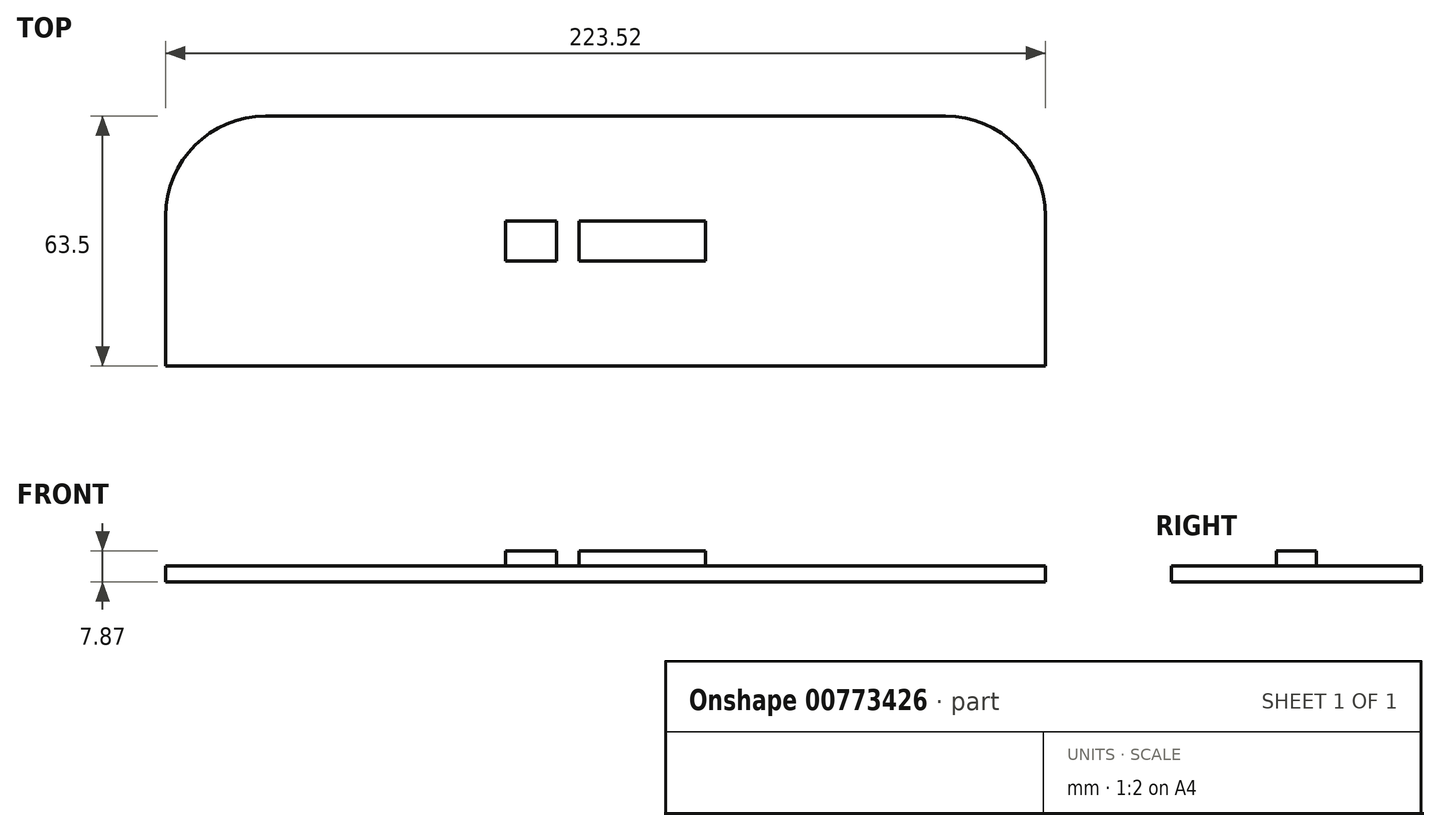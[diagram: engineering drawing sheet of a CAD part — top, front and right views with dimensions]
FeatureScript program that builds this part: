
annotation { "Feature Type Name" : "Feature", "Feature Type Description" : "" }
export const myFeature = defineFeature(function(context is Context, id is Id, definition is map)
    precondition{}
    {
        {
            var Q0;
            Q0=qCreatedBy(makeId("Top.planeOp"),FACE);
            var sketch = newSketch(context, id + "F0", { "sketchPlane" : qUnion([Q0])});
            skLineSegment(sketch, "E0.bottom", {"start": v(76.2, -38.1) * mm, "end": v(-76.2, -38.1) * mm});
            skLineSegment(sketch, "E0.top", {"start": v(76.2, 38.1) * mm, "end": v(-76.2, 38.1) * mm});
            skLineSegment(sketch, "E0.left", {"start": v(76.2, -38.1) * mm, "end": v(76.2, 38.1) * mm});
            skLineSegment(sketch, "E0.right", {"start": v(-76.2, -38.1) * mm, "end": v(-76.2, 38.1) * mm});
            skPoint(sketch, "E0.middle", {"position": v(0, 0) * mm});
            skSolve(sketch);
        }
        {
            var Q0;
            Q0=makeQuery(id+"F0.imprint","IMPRINT",FACE,{"disambiguationData":[TD([[makeQuery(id+"F0.imprint","IMPRINT",EDGE,{"derivedFrom":sQuery(id+"F0.wireOp",EDGE,"E0.bottom")}),-1.0]])]});
            extrude(context, id + "F1", {"entities" : qUnion([Q0]), "depth" : 10.16 * mm});
        }
        {
            var Q0;
            Q0=makeQuery(id+"F1.opExtrude","SWEPT_FACE",FACE,{"disambiguationData":[OSD([sQuery(id+"F0.wireOp",EDGE,"E0.bottom")])]});
            var sketch = newSketch(context, id + "F2", { "sketchPlane" : qUnion([Q0])});
            skCircle(sketch, "E1", {"center": v(-68.58, 7.62) * mm, "radius": 4 * mm});
            skCircle(sketch, "E2", {"center": v(-52.58, 7.62) * mm, "radius": 4 * mm});
            skSolve(sketch);
        }
        {
            var Q0;
            {var subQ0=sQuery(id+"F2.wireOp",EDGE,"E1");var subQ1=makeQuery(id+"F1.opExtrude","CAP_EDGE",EDGE,{"disambiguationData":[OSD([sQuery(id+"F0.wireOp",EDGE,"E0.bottom")])],"isStart":false});var subQ2=makeQuery(id+"F2.imprint","INTERSECT",VERTEX,{"disambiguationData":[OD(0.0)],"derivedFrom":[subQ1,subQ0]});Q0=makeQuery(id+"F2.imprint","IMPRINT",FACE,{"disambiguationData":[TD([[makeQuery(id+"F2.imprint","IMPRINT",EDGE,{"disambiguationData":[TD([[subQ2,-1.0]])],"derivedFrom":subQ0}),1.0]])]});}
            var Q1;
            {var subQ0=sQuery(id+"F2.wireOp",EDGE,"E2");var subQ1=makeQuery(id+"F1.opExtrude","CAP_EDGE",EDGE,{"disambiguationData":[OSD([sQuery(id+"F0.wireOp",EDGE,"E0.bottom")])],"isStart":false});var subQ2=makeQuery(id+"F2.imprint","INTERSECT",VERTEX,{"disambiguationData":[OD(0.0)],"derivedFrom":[subQ1,subQ0]});Q1=makeQuery(id+"F2.imprint","IMPRINT",FACE,{"disambiguationData":[TD([[makeQuery(id+"F2.imprint","IMPRINT",EDGE,{"disambiguationData":[TD([[subQ2,1.0]])],"derivedFrom":subQ0}),1.0]])]});}
            extrude(context, id + "F3", {"entities" : qUnion([Q0, Q1]), "operationType" : NewBodyOperationType.REMOVE, "oppositeDirection" : true, "depth" : 254 * mm});
        }
        {
            var Q0;
            Q0=makeQuery(id+"F1.opExtrude","CAP_FACE",FACE,{"disambiguationData":[OSD([sQuery(id+"F0.wireOp",EDGE,"E0.bottom"),sQuery(id+"F0.wireOp",EDGE,"E0.top"),sQuery(id+"F0.wireOp",EDGE,"E0.left"),sQuery(id+"F0.wireOp",EDGE,"E0.right")])],"isStart":true});
            var sketch = newSketch(context, id + "F4", { "sketchPlane" : qUnion([Q0])});
            skLineSegment(sketch, "E3.bottom", {"start": v(76.2, 38.1) * mm, "end": v(-38.1, 38.1) * mm});
            skLineSegment(sketch, "E3.top", {"start": v(76.2, -38.1) * mm, "end": v(-38.1, -38.1) * mm});
            skLineSegment(sketch, "E3.left", {"start": v(76.2, 38.1) * mm, "end": v(76.2, -38.1) * mm});
            skLineSegment(sketch, "E3.right", {"start": v(-38.1, 38.1) * mm, "end": v(-38.1, -38.1) * mm});
            skSolve(sketch);
        }
        {
            var Q0;
            Q0=makeQuery(id+"F4.imprint","IMPRINT",FACE,{"disambiguationData":[TD([[makeQuery(id+"F4.imprint","IMPRINT",EDGE,{"derivedFrom":sQuery(id+"F4.wireOp",EDGE,"E3.bottom")}),1.0]])]});
            extrude(context, id + "F5", {"entities" : qUnion([Q0]), "operationType" : NewBodyOperationType.REMOVE, "oppositeDirection" : true, "depth" : 5.08 * mm});
        }
        {
            var Q0;
            Q0=makeQuery(id+"F1.opExtrude","CAP_EDGE",EDGE,{"disambiguationData":[OSD([sQuery(id+"F0.wireOp",EDGE,"E0.right")])],"isStart":true});
            var Q1;
            Q1=makeQuery(id+"F5.boolean.opBoolean","COPY",EDGE,{"derivedFrom":makeQuery(id+"F5.opExtrude","CAP_EDGE",EDGE,{"disambiguationData":[OSD([sQuery(id+"F4.wireOp",EDGE,"E3.right")])],"isStart":true})});
            fillet(context, id + "F6", {"entities" : qUnion([Q0, Q1]), "radius" : 8.9 * mm, "tangentPropagation" : true, "allowEdgeOverflow" : false});
        }
        {
            var Q0;
            Q0=makeQuery(id+"F1.opExtrude","SWEPT_BODY",BODY,{"disambiguationData":[OSD([sQuery(id+"F0.wireOp",EDGE,"E0.bottom"),sQuery(id+"F0.wireOp",EDGE,"E0.top"),sQuery(id+"F0.wireOp",EDGE,"E0.left"),sQuery(id+"F0.wireOp",EDGE,"E0.right")])]});
            deleteBodies(context, id + "F7", {"entities" : qUnion([Q0])});
        }
        {
            var Q0;
            Q0=qCreatedBy(makeId("Top.planeOp"),FACE);
            var sketch = newSketch(context, id + "F8", { "sketchPlane" : qUnion([Q0])});
            skLineSegment(sketch, "E4.bottom", {"start": v(111.76, -31.75) * mm, "end": v(-111.76, -31.75) * mm});
            skLineSegment(sketch, "E4.top", {"start": v(111.76, 31.75) * mm, "end": v(-111.76, 31.75) * mm});
            skLineSegment(sketch, "E4.left", {"start": v(111.76, -31.75) * mm, "end": v(111.76, 31.75) * mm});
            skLineSegment(sketch, "E4.right", {"start": v(-111.76, -31.75) * mm, "end": v(-111.76, 31.75) * mm});
            skPoint(sketch, "E4.middle", {"position": v(0, 0) * mm});
            skSolve(sketch);
        }
        {
            var Q0;
            Q0=makeQuery(id+"F8.imprint","IMPRINT",FACE,{"disambiguationData":[TD([[makeQuery(id+"F8.imprint","IMPRINT",EDGE,{"derivedFrom":sQuery(id+"F8.wireOp",EDGE,"E4.bottom")}),-1.0]])]});
            extrude(context, id + "F9", {"entities" : qUnion([Q0]), "depth" : 2.8 * mm});
        }
        {
            var Q0;
            Q0=makeQuery(id+"F9.opExtrude","CAP_FACE",FACE,{"disambiguationData":[OSD([sQuery(id+"F8.wireOp",EDGE,"E4.bottom"),sQuery(id+"F8.wireOp",EDGE,"E4.top"),sQuery(id+"F8.wireOp",EDGE,"E4.left"),sQuery(id+"F8.wireOp",EDGE,"E4.right")])],"isStart":false});
            var sketch = newSketch(context, id + "F10", { "sketchPlane" : qUnion([Q0])});
            skLineSegment(sketch, "E5.bottom", {"start": v(25.4, -5.08) * mm, "end": v(-25.4, -5.08) * mm});
            skLineSegment(sketch, "E5.top", {"start": v(25.4, 5.08) * mm, "end": v(-25.4, 5.08) * mm});
            skLineSegment(sketch, "E5.left", {"start": v(25.4, -5.08) * mm, "end": v(25.4, 5.08) * mm});
            skLineSegment(sketch, "E5.right", {"start": v(-25.4, -5.08) * mm, "end": v(-25.4, 5.08) * mm});
            skPoint(sketch, "E5.middle", {"position": v(0, 0) * mm});
            skSolve(sketch);
        }
        {
            var Q0;
            Q0=makeQuery(id+"F10.imprint","IMPRINT",FACE,{"disambiguationData":[TD([[makeQuery(id+"F10.imprint","IMPRINT",EDGE,{"derivedFrom":sQuery(id+"F10.wireOp",EDGE,"E5.bottom")}),-1.0]])]});
            extrude(context, id + "F11", {"entities" : qUnion([Q0]), "operationType" : NewBodyOperationType.ADD, "depth" : 3.8 * mm});
        }
        {
            var Q0;
            Q0=makeQuery(id+"F11.opExtrude","SWEPT_FACE",FACE,{"disambiguationData":[OSD([sQuery(id+"F10.wireOp",EDGE,"E5.bottom")])]});
            var sketch = newSketch(context, id + "F12", { "sketchPlane" : qUnion([Q0])});
            skCircle(sketch, "E6", {"center": v(0, 5.59) * mm, "radius": 4.02 * mm});
            skCircle(sketch, "E7", {"center": v(18.84, 5.59) * mm, "radius": 4.02 * mm});
            skCircle(sketch, "E8", {"center": v(-18.84, 5.59) * mm, "radius": 4.02 * mm});
            skSolve(sketch);
        }
        {
            var Q0;
            {var subQ0=sQuery(id+"F12.wireOp",EDGE,"E6");var subQ1=sQuery(id+"F10.wireOp",EDGE,"E5.bottom");var subQ2=makeQuery(id+"F11.opExtrude","CAP_EDGE",EDGE,{"disambiguationData":[OSD([subQ1])],"isStart":false});var subQ3=makeQuery(id+"F12.imprint","INTERSECT",VERTEX,{"disambiguationData":[OD(0.0)],"derivedFrom":[subQ2,subQ0]});Q0=makeQuery(id+"F12.imprint","IMPRINT",FACE,{"disambiguationData":[TD([[makeQuery(id+"F12.imprint","IMPRINT",EDGE,{"disambiguationData":[TD([[subQ3,-1.0]])],"derivedFrom":subQ0}),1.0]])]});}
            var Q1;
            {var subQ0=sQuery(id+"F12.wireOp",EDGE,"E7");var subQ1=sQuery(id+"F10.wireOp",EDGE,"E5.bottom");var subQ2=makeQuery(id+"F11.opExtrude","CAP_EDGE",EDGE,{"disambiguationData":[OSD([subQ1])],"isStart":false});var subQ3=makeQuery(id+"F12.imprint","INTERSECT",VERTEX,{"disambiguationData":[OD(0.0)],"derivedFrom":[subQ2,subQ0]});Q1=makeQuery(id+"F12.imprint","IMPRINT",FACE,{"disambiguationData":[TD([[makeQuery(id+"F12.imprint","IMPRINT",EDGE,{"disambiguationData":[TD([[subQ3,-1.0]])],"derivedFrom":subQ0}),1.0]])]});}
            var Q2;
            {var subQ0=sQuery(id+"F12.wireOp",EDGE,"E6");var subQ1=makeQuery(id+"F11.opExtrude","CAP_EDGE",EDGE,{"disambiguationData":[OSD([sQuery(id+"F10.wireOp",EDGE,"E5.bottom")])],"isStart":true});var subQ2=makeQuery(id+"F12.imprint","INTERSECT",VERTEX,{"disambiguationData":[OD(0.0)],"derivedFrom":[subQ1,subQ0]});Q2=makeQuery(id+"F12.imprint","IMPRINT",FACE,{"disambiguationData":[TD([[makeQuery(id+"F12.imprint","IMPRINT",EDGE,{"disambiguationData":[TD([[subQ2,-1.0]])],"derivedFrom":subQ0}),1.0]])]});}
            var Q3;
            {var subQ0=sQuery(id+"F12.wireOp",EDGE,"E7");var subQ1=makeQuery(id+"F11.opExtrude","CAP_EDGE",EDGE,{"disambiguationData":[OSD([sQuery(id+"F10.wireOp",EDGE,"E5.bottom")])],"isStart":true});var subQ2=makeQuery(id+"F12.imprint","INTERSECT",VERTEX,{"disambiguationData":[OD(0.0)],"derivedFrom":[subQ1,subQ0]});Q3=makeQuery(id+"F12.imprint","IMPRINT",FACE,{"disambiguationData":[TD([[makeQuery(id+"F12.imprint","IMPRINT",EDGE,{"disambiguationData":[TD([[subQ2,-1.0]])],"derivedFrom":subQ0}),1.0]])]});}
            var Q4;
            {var subQ0=sQuery(id+"F12.wireOp",EDGE,"E8");var subQ1=sQuery(id+"F10.wireOp",EDGE,"E5.bottom");var subQ2=makeQuery(id+"F11.opExtrude","CAP_EDGE",EDGE,{"disambiguationData":[OSD([subQ1])],"isStart":false});var subQ3=makeQuery(id+"F12.imprint","INTERSECT",VERTEX,{"disambiguationData":[OD(0.0)],"derivedFrom":[subQ2,subQ0]});Q4=makeQuery(id+"F12.imprint","IMPRINT",FACE,{"disambiguationData":[TD([[makeQuery(id+"F12.imprint","IMPRINT",EDGE,{"disambiguationData":[TD([[subQ3,-1.0]])],"derivedFrom":subQ0}),1.0]])]});}
            var Q5;
            {var subQ0=sQuery(id+"F12.wireOp",EDGE,"E8");var subQ1=makeQuery(id+"F11.opExtrude","CAP_EDGE",EDGE,{"disambiguationData":[OSD([sQuery(id+"F10.wireOp",EDGE,"E5.bottom")])],"isStart":true});var subQ2=makeQuery(id+"F12.imprint","INTERSECT",VERTEX,{"disambiguationData":[OD(0.0)],"derivedFrom":[subQ1,subQ0]});Q5=makeQuery(id+"F12.imprint","IMPRINT",FACE,{"disambiguationData":[TD([[makeQuery(id+"F12.imprint","IMPRINT",EDGE,{"disambiguationData":[TD([[subQ2,-1.0]])],"derivedFrom":subQ0}),1.0]])]});}
            extrude(context, id + "F13", {"entities" : qUnion([Q0, Q1, Q2, Q3, Q4, Q5]), "operationType" : NewBodyOperationType.REMOVE, "endBound" : BoundingType.SYMMETRIC, "oppositeDirection" : true, "depth" : 127 * mm});
        }
        {
            var Q0;
            {var subQ0=sQuery(id+"F10.wireOp",EDGE,"E5.bottom");Q0=makeQuery(id+"F13.boolean.opBoolean","SPLIT",FACE,{"disambiguationData":[TD([makeQuery(id+"F9.opExtrude","CAP_FACE",FACE,{"disambiguationData":[OSD([sQuery(id+"F8.wireOp",EDGE,"E4.bottom"),sQuery(id+"F8.wireOp",EDGE,"E4.top"),sQuery(id+"F8.wireOp",EDGE,"E4.left"),sQuery(id+"F8.wireOp",EDGE,"E4.right")])],"isStart":false}),makeQuery(id+"F11.opExtrude","CAP_FACE",FACE,{"disambiguationData":[OSD([subQ0,sQuery(id+"F10.wireOp",EDGE,"E5.top"),sQuery(id+"F10.wireOp",EDGE,"E5.left"),sQuery(id+"F10.wireOp",EDGE,"E5.right")])],"isStart":false}),makeQuery(id+"F13.opExtrude","SWEPT_FACE",FACE,{"disambiguationData":[OSD([sQuery(id+"F12.wireOp",EDGE,"E6")])]}),makeQuery(id+"F13.opExtrude","SWEPT_FACE",FACE,{"disambiguationData":[OSD([sQuery(id+"F12.wireOp",EDGE,"E8")])]})])],"derivedFrom":makeQuery(id+"F11.opExtrude","SWEPT_FACE",FACE,{"disambiguationData":[OSD([subQ0])]})});}
            var sketch = newSketch(context, id + "F14", { "sketchPlane" : qUnion([Q0])});
            skLineSegment(sketch, "E9.bottom", {"start": v(-12.41, 6.6) * mm, "end": v(-6.7, 6.6) * mm});
            skLineSegment(sketch, "E9.top", {"start": v(-12.41, 2.8) * mm, "end": v(-6.7, 2.8) * mm});
            skLineSegment(sketch, "E9.left", {"start": v(-12.41, 6.6) * mm, "end": v(-12.41, 2.8) * mm});
            skLineSegment(sketch, "E9.right", {"start": v(-6.7, 6.6) * mm, "end": v(-6.7, 2.8) * mm});
            skLineSegment(sketch, "E10.bottom", {"start": v(6.7, 6.6) * mm, "end": v(12.41, 6.6) * mm});
            skLineSegment(sketch, "E10.top", {"start": v(6.7, 2.8) * mm, "end": v(12.41, 2.8) * mm});
            skLineSegment(sketch, "E10.left", {"start": v(6.7, 6.6) * mm, "end": v(6.7, 2.8) * mm});
            skLineSegment(sketch, "E10.right", {"start": v(12.41, 6.6) * mm, "end": v(12.41, 2.8) * mm});
            skSolve(sketch);
        }
        {
            var Q0;
            Q0=makeQuery(id+"F14.imprint","IMPRINT",FACE,{"disambiguationData":[TD([[makeQuery(id+"F14.imprint","IMPRINT",EDGE,{"derivedFrom":sQuery(id+"F14.wireOp",EDGE,"E9.bottom")}),1.0]])]});
            var Q1;
            Q1=makeQuery(id+"F14.imprint","IMPRINT",FACE,{"disambiguationData":[TD([[makeQuery(id+"F14.imprint","IMPRINT",EDGE,{"derivedFrom":sQuery(id+"F14.wireOp",EDGE,"E10.bottom")}),-1.0]])]});
            extrude(context, id + "F15", {"entities" : qUnion([Q0, Q1]), "operationType" : NewBodyOperationType.REMOVE, "oppositeDirection" : true, "depth" : 25.4 * mm});
        }
        {
            var Q0;
            Q0=makeQuery(id+"F9.opExtrude","SWEPT_EDGE",EDGE,{"disambiguationData":[OSD([sQuery(id+"F8.wireOp",EDGE,"E4.top"),sQuery(id+"F8.wireOp",EDGE,"E4.left")])]});
            var Q1;
            Q1=makeQuery(id+"F9.opExtrude","SWEPT_EDGE",EDGE,{"disambiguationData":[OSD([sQuery(id+"F8.wireOp",EDGE,"E4.top"),sQuery(id+"F8.wireOp",EDGE,"E4.right")])]});
            fillet(context, id + "F16", {"entities" : qUnion([Q0, Q1]), "radius" : 25.4 * mm, "tangentPropagation" : true, "allowEdgeOverflow" : false});
        }
        {
            var Q0;
            Q0=makeQuery(id+"F9.opExtrude","CAP_FACE",FACE,{"disambiguationData":[OSD([sQuery(id+"F8.wireOp",EDGE,"E4.bottom"),sQuery(id+"F8.wireOp",EDGE,"E4.top"),sQuery(id+"F8.wireOp",EDGE,"E4.left"),sQuery(id+"F8.wireOp",EDGE,"E4.right")])],"isStart":true});
            extrude(context, id + "F17", {"entities" : qUnion([Q0]), "operationType" : NewBodyOperationType.ADD, "depth" : 1.27 * mm});
        }
    });
